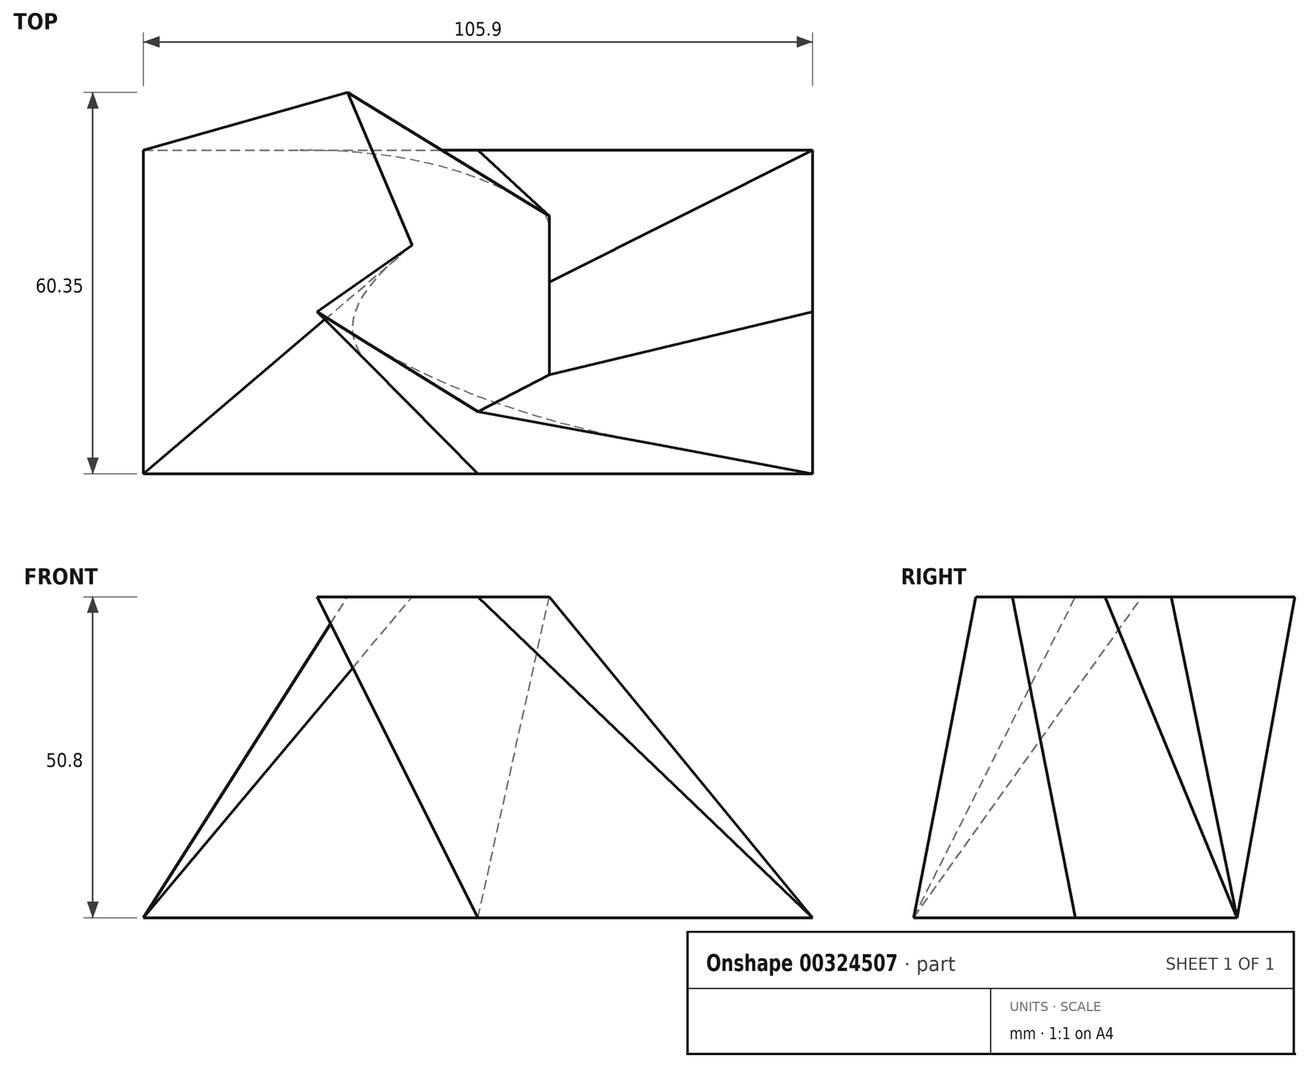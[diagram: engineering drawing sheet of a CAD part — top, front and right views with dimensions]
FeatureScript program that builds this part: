
annotation { "Feature Type Name" : "Feature", "Feature Type Description" : "" }
export const myFeature = defineFeature(function(context is Context, id is Id, definition is map)
    precondition{}
    {
        {
            var Q0;
            Q0=qCreatedBy(makeId("Top.planeOp"),FACE);
            var sketch = newSketch(context, id + "F0", { "sketchPlane" : qUnion([Q0])});
            skLineSegment(sketch, "E0.bottom", {"start": v(-52.95, 25.6) * mm, "end": v(52.95, 25.6) * mm});
            skLineSegment(sketch, "E0.top", {"start": v(-52.95, -25.6) * mm, "end": v(52.95, -25.6) * mm});
            skLineSegment(sketch, "E0.left", {"start": v(-52.95, 25.6) * mm, "end": v(-52.95, -25.6) * mm});
            skLineSegment(sketch, "E0.right", {"start": v(52.95, 25.6) * mm, "end": v(52.95, -25.6) * mm});
            skPoint(sketch, "E0.middle", {"position": v(0, 0) * mm});
            skSolve(sketch);
        }
        {
            var Q0;
            Q0=qCreatedBy(makeId("Top.planeOp"),FACE);
            cPlane(context, id + "F1", {"entities" : qUnion([Q0]), "cplaneType" : CPlaneType.OFFSET, "offset" : 50.8 * mm, "width" : 152.4 * mm, "height" : 152.4 * mm});
        }
        {
            var Q0;
            Q0=qCreatedBy(id+"F1.planeOp",FACE);
            var sketch = newSketch(context, id + "F2", { "sketchPlane" : qUnion([Q0])});
            skPoint(sketch, "E1", {"position": v(0, 0) * mm});
            skLineSegment(sketch, "E2", {"start": v(0, -15.77) * mm, "end": v(-25.46, 0) * mm});
            skLineSegment(sketch, "E3", {"start": v(-25.46, 0) * mm, "end": v(-10.42, 10.56) * mm});
            skLineSegment(sketch, "E4", {"start": v(11.29, 4.72) * mm, "end": v(11.29, -9.98) * mm});
            skLineSegment(sketch, "E5", {"start": v(11.29, -9.98) * mm, "end": v(0, -15.77) * mm});
            skLineSegment(sketch, "E6", {"start": v(-10.42, 10.56) * mm, "end": v(-20.63, 34.74) * mm});
            skLineSegment(sketch, "E7", {"start": v(-20.63, 34.74) * mm, "end": v(11.29, 15.2) * mm});
            skLineSegment(sketch, "E8", {"start": v(11.29, 4.72) * mm, "end": v(11.29, 15.2) * mm});
            skSolve(sketch);
        }
        {
            var Q0;
            Q0=makeQuery(id+"F0.imprint","IMPRINT",FACE,{"disambiguationData":[TD([[makeQuery(id+"F0.imprint","IMPRINT",EDGE,{"derivedFrom":sQuery(id+"F0.wireOp",EDGE,"E0.bottom")}),-1.0]])]});
            var Q1;
            Q1=makeQuery(id+"F2.imprint","IMPRINT",FACE,{"disambiguationData":[TD([[makeQuery(id+"F2.imprint","IMPRINT",EDGE,{"derivedFrom":sQuery(id+"F2.wireOp",EDGE,"E2")}),-1.0]])]});
            loft(context, id + "F3", {"sheetProfilesArray" : [{ "sheetProfileEntities" : qUnion([Q0]) }, { "sheetProfileEntities" : qUnion([Q1]) }]});
        }
    });
